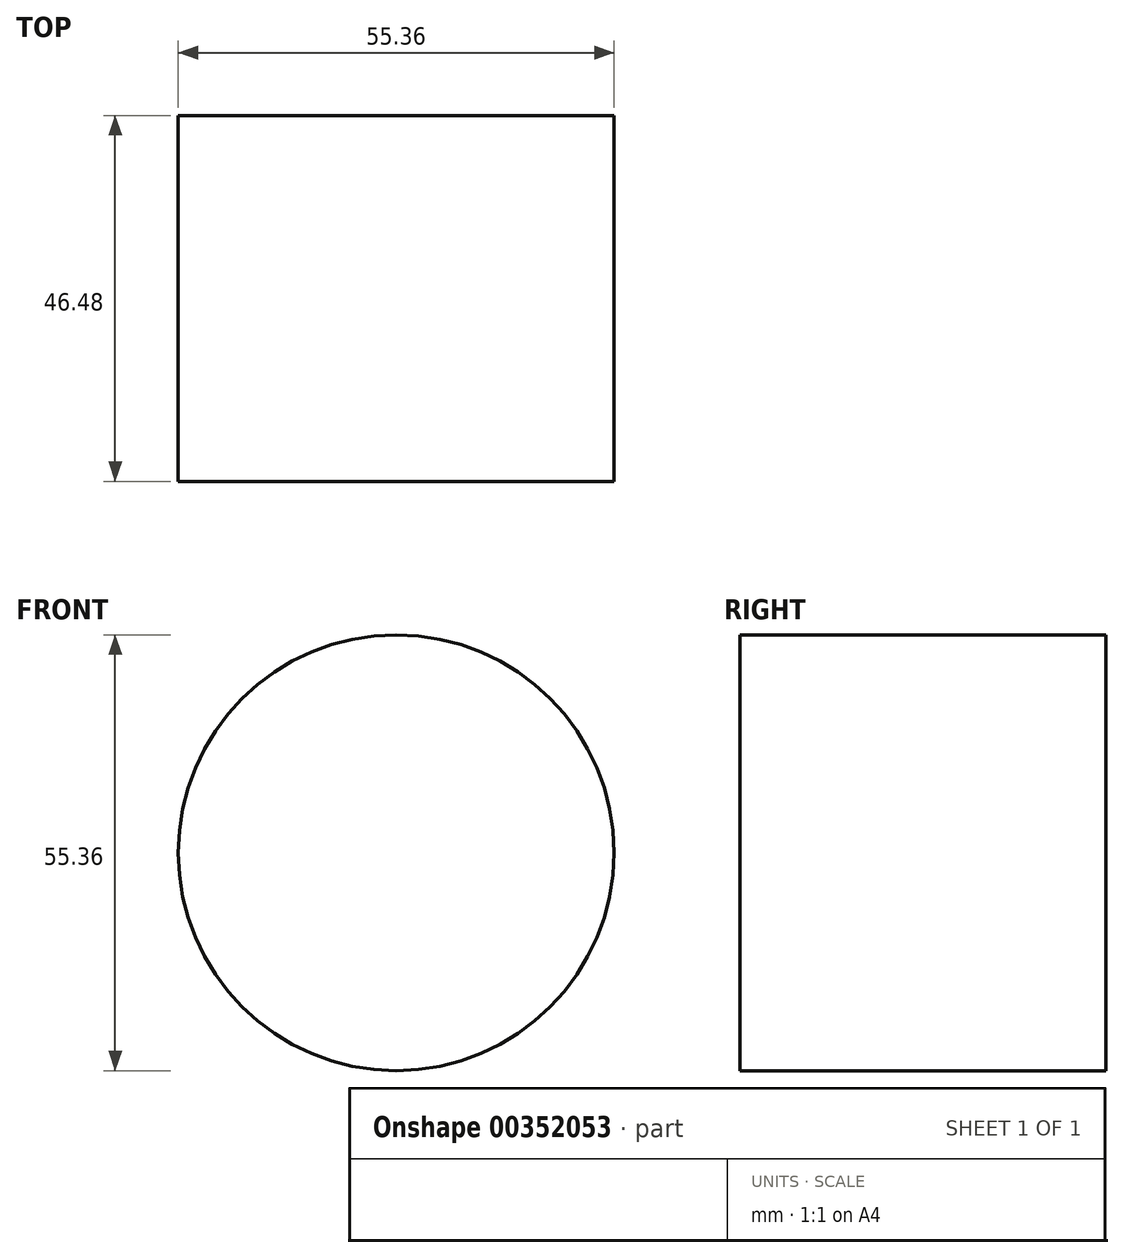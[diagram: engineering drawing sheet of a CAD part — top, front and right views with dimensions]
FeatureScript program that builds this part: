
annotation { "Feature Type Name" : "Feature", "Feature Type Description" : "" }
export const myFeature = defineFeature(function(context is Context, id is Id, definition is map)
    precondition{}
    {
        {
            var Q0;
            Q0=qCreatedBy(makeId("Front.planeOp"),FACE);
            var sketch = newSketch(context, id + "F0", { "sketchPlane" : qUnion([Q0])});
            skCircle(sketch, "E0", {"center": v(0.67, 0) * mm, "radius": 27.68 * mm});
            skSolve(sketch);
        }
        {
            var Q0;
            Q0 = qSketchRegion(id + "F0", true);
            extrude(context, id + "F1", {"entities" : qUnion([Q0]), "depth" : 46.48 * mm});
        }
    });
